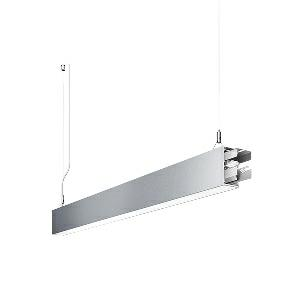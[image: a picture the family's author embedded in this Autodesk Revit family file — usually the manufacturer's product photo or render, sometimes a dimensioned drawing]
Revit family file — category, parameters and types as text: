
# Revit family: idoo_line_-_ilp_4000_vtl_d_sta_00806469_cd0f
name_source: partatom
category: Lighting Fixtures
units: mm (PartAtom-declared; Revit-internal decimal feet)

## family parameters
Cut with Voids When Loaded = No
Host = Face
Light Source = No
Part Type = Normal
Room Calculation Point = No
Round Connector Dimension = Use Diameter
Shared = No

## types (1)
- IDOO.line - ILP 4000/VTL/D STA (1 x LED, 3850 lm, 2700-6500K)
    Apparent Load = 39 VA
    Approval mark = CE
    CIE Flux Codes = 66 91 98 40 100
    Color Rendering = 90-100
    Color Temperature = 2700-6500K
    Control Gear = Electronic ballast
    Default Elevation = 1800 mm
    Description = ILP 4000/VTL/D|Suspended luminaire|light source: LED|connected load: 220-240 V, 50/60 Hz|Power consumption: approx. 39 W|standby: approx. 0,25|luminous flux: 3850 lm|luminous efficacy: 98 lm/W|light distribution: Direct/indirect|direct ratio: approx. 40 %|colour temperature: Cold white, ca. 2700-6500 K|color rendering index (CRI): >= 90|chromaticity tolerance:  3 SDCM|System of protection: IP 40|technology: Continuously dimmable|luminaire body|material: Sectional aluminium|colour: Silver|lamp cover: Acrylic (PMMA), Clear|mains lead: 2.00 m With free stranded wires|Fastening: Steel cable 0.3 - 0.7 m|glare control: Prism aperture|luminance(L65): <= 2700 cd/m|unified glare rating(4H 8H): <=  16|special features: Specified values at approx. 4000 K, DALI Load 1x, Through-wired, up to 18 m on one mains connection, External control required for Dali Device type 8, Flicker-free, Constant luminous flux between 2700 and 6500 K, Constant colour temperature over the whole dimming range, Suitable as emergency lighting, Start luminaire with mains connection, Mechanical and electrical connection of the individual modules without tools|
    Frequency = 50 Hz
    Height = 110 mm
    Lamp = 1 x LED
    Lamp Light Flux = 3850 lm
    Lamp count = 1
    Length = 1408 mm
    Luminous efficacy = 99 lm/W
    Manufacturer = Waldmann
    ModVariant = No
    Model = 00806469
    Mounting Place = Ceiling
    Mounting Type = Pendant
    Number of Poles = 1
    OnlyDefault = Yes
    Power Factor = 1
    Product Name = IDOO.line - ILP 4000/VTL/D STA
    Product group = Suspended luminaire
    ProductGroupID = 9
    Protection Class = Protection class I
    Protection Degree = IP 40
    RLX_Detail_Level = 1
    RLX_Emergency_Light_Flux = 0 lm
    RLX_Emergency_Type = 0
    RLX_Emergency_Type_DB = No
    RlxData = <blob elided: 23821 chars, md5=cf7676ad>
    Socket = socket
    Standby Power = 0 W
    System Light Flux = 3850 lm
    System Power = 39 W
    Type Comments = Product without accessories
    Type Image = 113310000-00692594.jpg
    URL = http://relux.com
    VarID = ---
    Voltage = 230 V
    Voltage Range = 220-240 V
    Weight = 0.00 kg
    Width = 60 mm  [stored 0.19685 ft]

note: [stored X ft] marks values corroborated as IEEE doubles in the binary element streams (Revit-internal decimal feet)

## geometry (parser evidence)
native form markers: Blend x4, Sweep x15
no freeform markers — native parametric forms only
